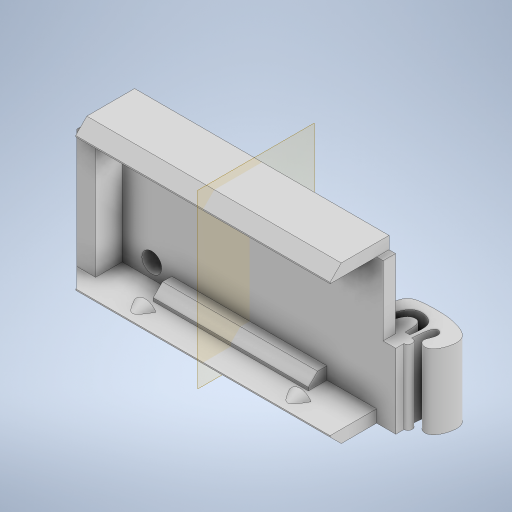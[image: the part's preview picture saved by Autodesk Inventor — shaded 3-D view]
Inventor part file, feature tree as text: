
AUTODESK INVENTOR PART (.ipt)
format: ipt  version: 2023 (Build 270158030, 158C)  size: 668,160 bytes
history: native  units: mm
features: extrude x11, sketch x8, other x6, chamfer x6, projected_geometry x6, plane x3, mirror x3, reference x1
ambient origin geometry x8: Origin, YZ Plane, XZ Plane, XY Plane, X Axis, Y Axis, Z Axis, Center Point
bodies: Solid1 (feature_tree)
feature tree (44):
  other  "Blocks"
  sketch  "Sketch1"  dims[d0=2.0mm d1=0.0mm d4=10.0mm d5=0.0mm]
  extrude  "Extrusion1"  Depth=10.0mm TaperAngle=0.0deg
  plane  "Work Plane1"
  extrude  "Extrusion2"  Depth=3.0mm
  mirror  "Mirror1"
  extrude  "Extrusion6"  Depth=17.780726mm
  extrude  "Extrusion16"  Depth=6.409146mm
  extrude  "Extrusion8"  Depth=1.257608mm
  mirror  "Mirror2"
  extrude  "Extrusion9"  Depth=0.803745mm
  plane  "Work Plane10"
  extrude  "Extrusion11"  Depth=0.7465mm
  extrude  "Extrusion12"  TaperAngle=0.0deg  [1 undecoded]
  mirror  "Mirror3"
  extrude  "Extrusion13"  Depth=2.0mm TaperAngle=0.0deg
  chamfer  "Chamfer5"  Distance=10.0mm
  chamfer  "Chamfer6"  Distance=1.3mm
  chamfer  "Chamfer7"  Distance=4.0mm
  plane  "Work Plane5"
  extrude  "Extrusion14"  Depth=4.3mm
  extrude  "Extrusion15"  Depth=4.3mm TaperAngle=0.0deg
  chamfer  "Chamfer9"  [1 undecoded]
  chamfer  "Chamfer10"  Distance=2.0mm Angle=45.0deg
  chamfer  "Chamfer11"  Distance=2.0mm Angle=45.0deg
  reference  "Reference1"
  sketch  "Sketch2"  dims[d41=23.55mm d43=3.0mm]
  other  "DIN-rail-mount"
  sketch  "Sketch6"  dims[d44=0.5mm d45=17.780726mm]
  sketch  "Sketch9"  dims[d46=4.630585mm d47=6.409146mm]
  sketch  "Sketch13"  dims[d48=0.917895mm d49=1.257608mm]
  sketch  "Sketch14"  dims[d50=1.460869mm d51=0.803745mm]
  sketch  "Sketch15"  dims[d52=2.954284mm d53=0.7465mm]
  other  "board"
  sketch  "Sketch16"  dims[d54=0.593847mm d55=0.0mm d56=0.0mm d61=2.0mm d62=0.0mm d65=10.0mm d66=0.0mm d67=1.3mm d76=4.0mm d78=12.0mm d79=-4.537856mm d80=12.0mm d81=0.0mm d82=0.0mm d83=0.0mm d84=1.8mm d85=2.0mm d86=45.0deg d88=1.5mm d89=2.0mm d90=45.0deg d91=1.5mm d92=2.0mm d93=45.0deg d97=21.0mm d98=43.0mm d99=1.3mm d100=0.0mm d101=1.3mm d102=0.0mm d103=3.0mm d104=2.0mm d105=45.0deg d106=2.0mm d107=2.0mm d108=45.0deg d109=2.0mm d110=2.0mm d111=45.0deg d117=3.0mm d123=16.819631mm d124=17.830248mm d125=16.711144mm d126=0.704136mm d127=16.322468mm d128=0.003807mm d129=4.370885mm d130=0.289941mm d131=0.003807mm d132=18.518058mm d133=20.70572mm d134=22.811962mm d135=22.890117mm d136=0.608753mm d137=23.48774mm d138=0.990364mm d149=17.5mm d150=41.0mm d151=3.0mm d152=3.1mm d153=2.0mm d154=2.0mm d155=0.0mm d156=8.0mm d157=8.0mm d158=3.0mm d159=1.3mm d164=8.0mm d165=8.0mm d166=4.3mm]
  projected_geometry  "Projected Loop9"
  projected_geometry  "Projected Loop11"
  projected_geometry  "Projected Loop12"
  projected_geometry  "Projected Loop13"
  projected_geometry  "Projected Loop14"
  projected_geometry  "Projected Loop15"
  other  "buck-converter-din-rail-mount.iam"
  other  "Power Buck Converter:1"
  other  "DIN-rail-mount:1"
note: 2 required parameter values undecoded (feature->parameter linkage not recoverable at this tier; creation-order binding heuristic only, values carry confidence <= 0.55)
